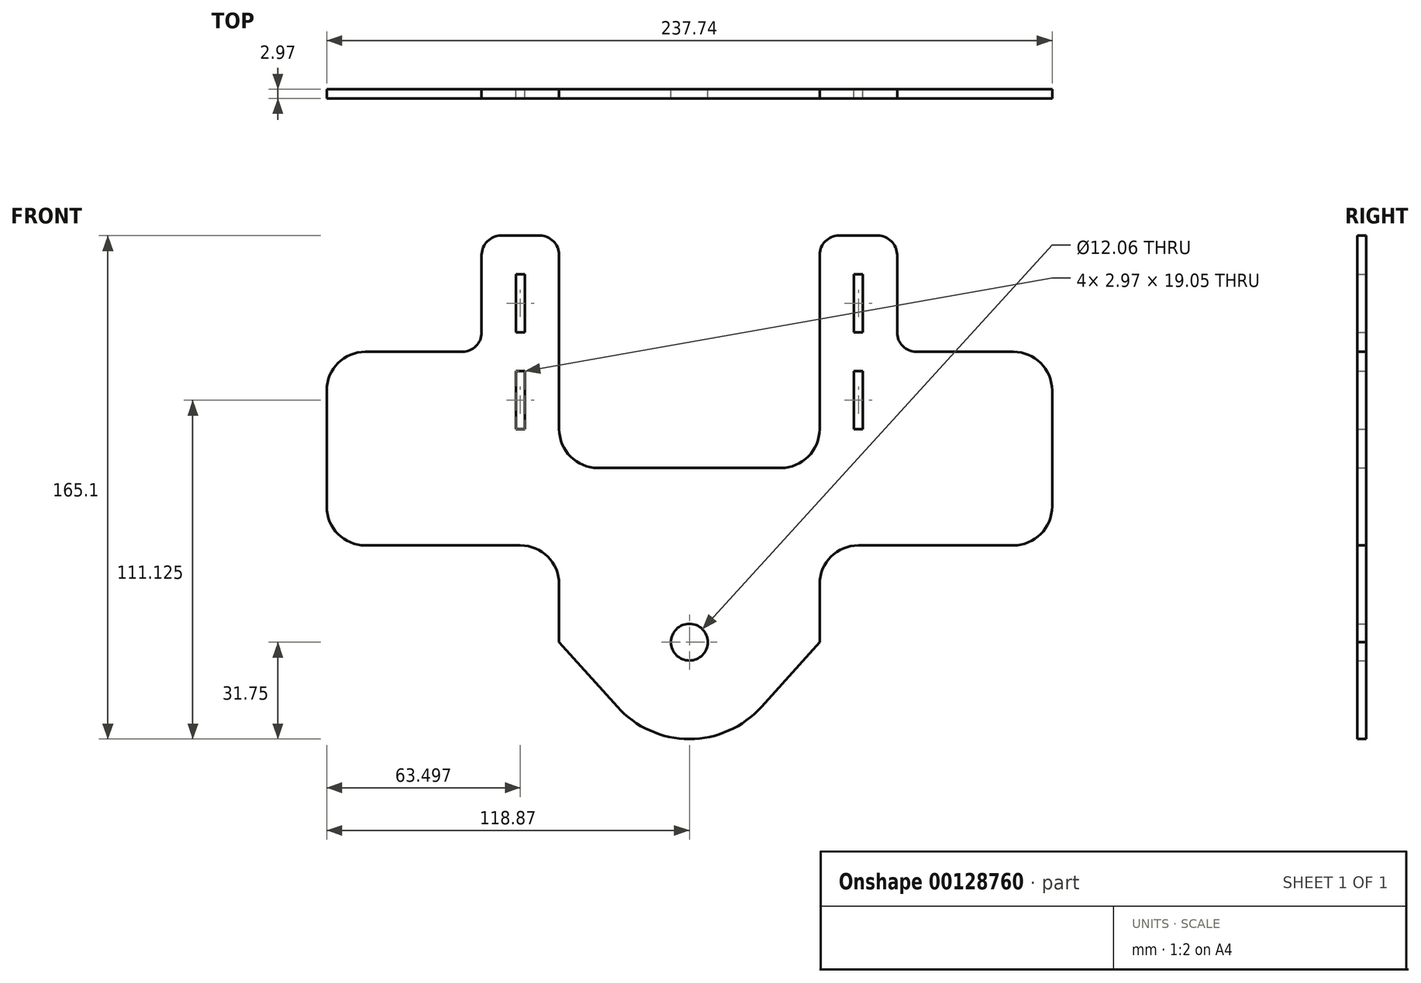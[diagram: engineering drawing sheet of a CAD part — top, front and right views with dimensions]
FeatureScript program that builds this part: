
annotation { "Feature Type Name" : "Feature", "Feature Type Description" : "" }
export const myFeature = defineFeature(function(context is Context, id is Id, definition is map)
    precondition{}
    {
        {
            var Q0;
            Q0=qCreatedBy(makeId("Front.planeOp"),FACE);
            var sketch = newSketch(context, id + "F0", { "sketchPlane" : qUnion([Q0])});
            skCircle(sketch, "E0", {"center": v(0, 0) * mm, "radius": 31.75 * mm});
            skPoint(sketch, "E1", {"position": v(0, -31.75) * mm});
            skLineSegment(sketch, "E2", {"start": v(-23.62, -21.21) * mm, "end": v(-42.67, 0) * mm});
            skLineSegment(sketch, "E3", {"start": v(23.62, -21.21) * mm, "end": v(42.67, 0) * mm});
            skLineSegment(sketch, "E4", {"start": v(-42.67, 127) * mm, "end": v(-42.67, 69.85) * mm});
            skLineSegment(sketch, "E5", {"start": v(-29.97, 57.15) * mm, "end": v(29.97, 57.15) * mm});
            skLineSegment(sketch, "E6", {"start": v(42.67, 69.85) * mm, "end": v(42.67, 127) * mm});
            skLineSegment(sketch, "E7.bottom", {"start": v(-56.86, 120.65) * mm, "end": v(-53.89, 120.65) * mm});
            skLineSegment(sketch, "E7.top", {"start": v(-56.86, 101.6) * mm, "end": v(-53.89, 101.6) * mm});
            skLineSegment(sketch, "E7.left", {"start": v(-56.86, 120.65) * mm, "end": v(-56.86, 101.6) * mm});
            skLineSegment(sketch, "E7.right", {"start": v(-53.89, 120.65) * mm, "end": v(-53.89, 101.6) * mm});
            skLineSegment(sketch, "E8.bottom", {"start": v(-56.86, 88.9) * mm, "end": v(-53.89, 88.9) * mm});
            skLineSegment(sketch, "E8.top", {"start": v(-56.86, 69.85) * mm, "end": v(-53.89, 69.85) * mm});
            skLineSegment(sketch, "E8.left", {"start": v(-56.86, 88.9) * mm, "end": v(-56.86, 69.85) * mm});
            skLineSegment(sketch, "E8.right", {"start": v(-53.89, 88.9) * mm, "end": v(-53.89, 69.85) * mm});
            skLineSegment(sketch, "E9.bottom", {"start": v(53.89, 120.65) * mm, "end": v(56.86, 120.65) * mm});
            skLineSegment(sketch, "E9.top", {"start": v(53.89, 101.6) * mm, "end": v(56.86, 101.6) * mm});
            skLineSegment(sketch, "E9.left", {"start": v(53.89, 120.65) * mm, "end": v(53.89, 101.6) * mm});
            skLineSegment(sketch, "E9.right", {"start": v(56.86, 120.65) * mm, "end": v(56.86, 101.6) * mm});
            skLineSegment(sketch, "E10.bottom", {"start": v(53.89, 88.9) * mm, "end": v(56.86, 88.9) * mm});
            skLineSegment(sketch, "E10.top", {"start": v(53.89, 69.85) * mm, "end": v(56.86, 69.85) * mm});
            skLineSegment(sketch, "E10.left", {"start": v(53.89, 88.9) * mm, "end": v(53.89, 69.85) * mm});
            skLineSegment(sketch, "E10.right", {"start": v(56.86, 88.9) * mm, "end": v(56.86, 69.85) * mm});
            skPoint(sketch, "E11", {"position": v(0, 57.15) * mm});
            skLineSegment(sketch, "E12", {"start": v(-55.37, 120.65) * mm, "end": v(-55.37, 69.85) * mm, "construction": true});
            skLineSegment(sketch, "E13", {"start": v(55.37, 120.65) * mm, "end": v(55.37, 69.85) * mm, "construction": true});
            skPoint(sketch, "E14", {"position": v(-55.37, 69.85) * mm});
            skPoint(sketch, "E15", {"position": v(-55.37, 95.25) * mm});
            skPoint(sketch, "E16", {"position": v(55.37, 95.25) * mm});
            skPoint(sketch, "E17.orphan", {"position": v(0, 31.75) * mm});
            skLineSegment(sketch, "E18", {"start": v(-42.67, 0) * mm, "end": v(-42.67, 19.05) * mm});
            skLineSegment(sketch, "E19", {"start": v(42.67, 0) * mm, "end": v(42.67, 19.05) * mm});
            skLineSegment(sketch, "E20", {"start": v(-55.37, 31.75) * mm, "end": v(-106.17, 31.75) * mm});
            skLineSegment(sketch, "E21", {"start": v(-49.02, 133.35) * mm, "end": v(-61.72, 133.35) * mm});
            skLineSegment(sketch, "E22", {"start": v(-68.07, 127) * mm, "end": v(-68.07, 101.6) * mm});
            skPoint(sketch, "E23", {"position": v(-68.07, 31.75) * mm});
            skLineSegment(sketch, "E24", {"start": v(-118.87, 44.45) * mm, "end": v(-118.87, 82.55) * mm});
            skLineSegment(sketch, "E25", {"start": v(-106.17, 95.25) * mm, "end": v(-74.42, 95.25) * mm});
            skPoint(sketch, "E26.visualSharp", {"position": v(-118.87, 95.25) * mm});
            skArc(sketch, "E26.filletArc", {"start": v(-106.17, 95.25) * mm, "mid": v(-115.15, 91.53) * mm, "end": v(-118.87, 82.55) * mm});
            skPoint(sketch, "E27.visualSharp", {"position": v(-118.87, 31.75) * mm});
            skArc(sketch, "E27.filletArc", {"start": v(-118.87, 44.45) * mm, "mid": v(-115.15, 35.47) * mm, "end": v(-106.17, 31.75) * mm});
            skPoint(sketch, "E28.visualSharp", {"position": v(-42.67, 31.75) * mm});
            skArc(sketch, "E28.filletArc", {"start": v(-42.67, 19.05) * mm, "mid": v(-46.4, 28.03) * mm, "end": v(-55.37, 31.75) * mm});
            skPoint(sketch, "E29.visualSharp", {"position": v(-68.07, 133.35) * mm});
            skArc(sketch, "E29.filletArc", {"start": v(-61.72, 133.35) * mm, "mid": v(-66.21, 131.5) * mm, "end": v(-68.07, 127) * mm});
            skPoint(sketch, "E30.visualSharp", {"position": v(-42.67, 133.35) * mm});
            skArc(sketch, "E30.filletArc", {"start": v(-42.67, 127) * mm, "mid": v(-44.53, 131.5) * mm, "end": v(-49.02, 133.35) * mm});
            skLineSegment(sketch, "E31", {"start": v(55.37, 31.75) * mm, "end": v(106.17, 31.75) * mm});
            skLineSegment(sketch, "E32", {"start": v(118.87, 44.45) * mm, "end": v(118.87, 82.55) * mm});
            skLineSegment(sketch, "E33", {"start": v(106.17, 95.25) * mm, "end": v(74.42, 95.25) * mm});
            skLineSegment(sketch, "E34", {"start": v(68.07, 101.6) * mm, "end": v(68.07, 127) * mm});
            skLineSegment(sketch, "E35", {"start": v(61.72, 133.35) * mm, "end": v(49.02, 133.35) * mm});
            skPoint(sketch, "E36.visualSharp", {"position": v(42.67, 31.75) * mm});
            skArc(sketch, "E36.filletArc", {"start": v(55.37, 31.75) * mm, "mid": v(46.4, 28.03) * mm, "end": v(42.67, 19.05) * mm});
            skPoint(sketch, "E37.visualSharp", {"position": v(118.87, 31.75) * mm});
            skArc(sketch, "E37.filletArc", {"start": v(106.17, 31.75) * mm, "mid": v(115.15, 35.47) * mm, "end": v(118.87, 44.45) * mm});
            skPoint(sketch, "E38.visualSharp", {"position": v(118.87, 95.25) * mm});
            skArc(sketch, "E38.filletArc", {"start": v(118.87, 82.55) * mm, "mid": v(115.15, 91.53) * mm, "end": v(106.17, 95.25) * mm});
            skPoint(sketch, "E39.visualSharp", {"position": v(42.67, 133.35) * mm});
            skArc(sketch, "E39.filletArc", {"start": v(49.02, 133.35) * mm, "mid": v(44.53, 131.5) * mm, "end": v(42.67, 127) * mm});
            skPoint(sketch, "E40.visualSharp", {"position": v(68.07, 133.35) * mm});
            skArc(sketch, "E40.filletArc", {"start": v(68.07, 127) * mm, "mid": v(66.21, 131.5) * mm, "end": v(61.72, 133.35) * mm});
            skPoint(sketch, "E41.visualSharp", {"position": v(-68.07, 95.25) * mm});
            skArc(sketch, "E41.filletArc", {"start": v(-74.42, 95.25) * mm, "mid": v(-69.93, 97.1) * mm, "end": v(-68.07, 101.6) * mm});
            skPoint(sketch, "E42.visualSharp", {"position": v(68.07, 95.25) * mm});
            skArc(sketch, "E42.filletArc", {"start": v(68.07, 101.6) * mm, "mid": v(69.93, 97.1) * mm, "end": v(74.42, 95.25) * mm});
            skPoint(sketch, "E43.visualSharp", {"position": v(-42.67, 57.15) * mm});
            skArc(sketch, "E43.filletArc", {"start": v(-42.67, 69.85) * mm, "mid": v(-38.95, 60.87) * mm, "end": v(-29.97, 57.15) * mm});
            skPoint(sketch, "E44.visualSharp", {"position": v(42.67, 57.15) * mm});
            skArc(sketch, "E44.filletArc", {"start": v(29.97, 57.15) * mm, "mid": v(38.95, 60.87) * mm, "end": v(42.67, 69.85) * mm});
            skCircle(sketch, "E45", {"center": v(0, 0) * mm, "radius": 6.03 * mm});
            skSolve(sketch);
        }
        {
            var Q0;
            {var subQ0=sQuery(id+"F0.wireOp",EDGE,"E2");Q0=makeQuery(id+"F0.imprint","IMPRINT",FACE,{"disambiguationData":[TD([[makeQuery(id+"F0.imprint","IMPRINT",EDGE,{"derivedFrom":subQ0}),-1.0]])]});}
            var Q1;
            {var subQ0=sQuery(id+"F0.wireOp",EDGE,"E0");var subQ1=makeQuery(id+"F0.imprint","INTERSECT",VERTEX,{"derivedFrom":[subQ0,sQuery(id+"F0.wireOp",EDGE,"E2")]});Q1=makeQuery(id+"F0.imprint","IMPRINT",FACE,{"disambiguationData":[TD([[makeQuery(id+"F0.imprint","IMPRINT",EDGE,{"disambiguationData":[TD([[subQ1,-1.0]])],"derivedFrom":subQ0}),1.0]])]});}
            extrude(context, id + "F1", {"entities" : qUnion([Q0, Q1]), "depth" : 2.97 * mm});
        }
    });
